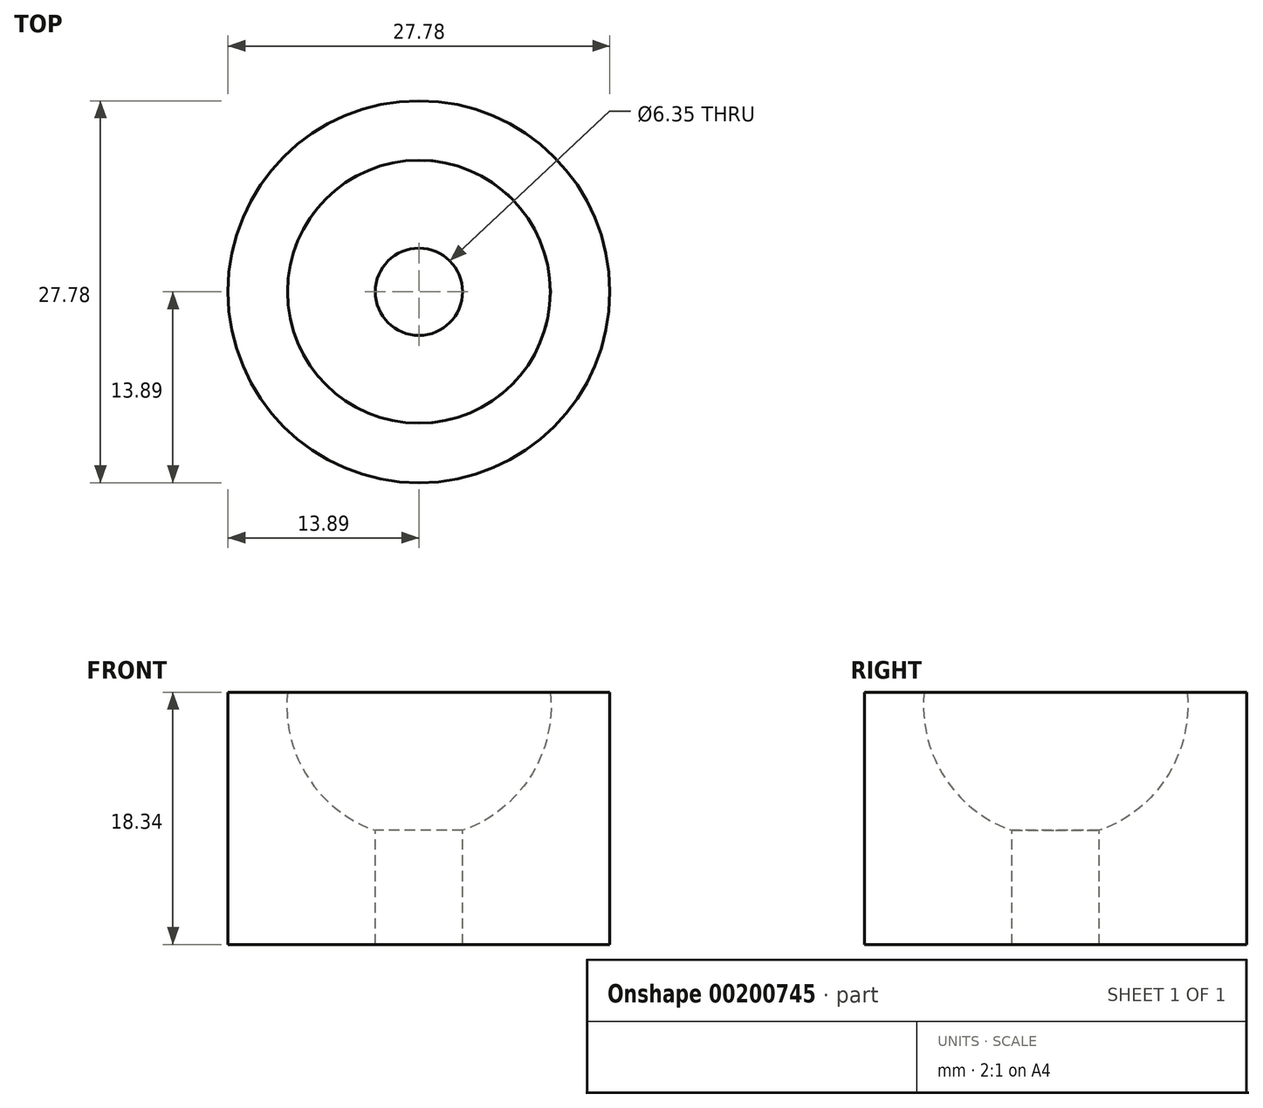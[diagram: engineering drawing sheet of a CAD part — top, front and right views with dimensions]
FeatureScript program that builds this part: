
annotation { "Feature Type Name" : "Feature", "Feature Type Description" : "" }
export const myFeature = defineFeature(function(context is Context, id is Id, definition is map)
    precondition{}
    {
        {
            var Q0;
            Q0=qCreatedBy(makeId("Front.planeOp"),FACE);
            var sketch = newSketch(context, id + "F0", { "sketchPlane" : qUnion([Q0])});
            skArc(sketch, "E0", {"start": v(-9.56, -0.66) * mm, "mid": v(-7.14, -8.08) * mm, "end": v(0, -11.25) * mm});
            skArc(sketch, "E1", {"start": v(0, -11.25) * mm, "mid": v(7.14, 4.8) * mm, "end": v(-9.56, -0.66) * mm, "construction": true});
            skLineSegment(sketch, "E2", {"start": v(-9.56, -0.66) * mm, "end": v(-13.9, -0.66) * mm});
            skLineSegment(sketch, "E3", {"start": v(-13.9, -0.66) * mm, "end": v(-13.9, -19) * mm});
            skLineSegment(sketch, "E4", {"start": v(-13.9, -19) * mm, "end": v(0, -19) * mm});
            skLineSegment(sketch, "E5", {"start": v(0, -11.25) * mm, "end": v(0, -19) * mm});
            skSolve(sketch);
        }
        {
            var Q0;
            Q0=makeQuery(id+"F0.imprint","IMPRINT",FACE,{"disambiguationData":[TD([[makeQuery(id+"F0.imprint","IMPRINT",EDGE,{"derivedFrom":sQuery(id+"F0.wireOp",EDGE,"E0")}),-1.0]])]});
            var Q1;
            Q1 = qSketchRegion(id + "F2", true);
            var Q2;
            Q2=sQuery(id+"F0.wireOp",EDGE,"E5");
            revolve(context, id + "F1", {"entities" : qUnion([Q0, Q1]), "axis" : qUnion([Q2]), "revolveType" : RevolveType.FULL});
        }
        {
            var Q0;
            Q0=qCreatedBy(makeId("Top.planeOp"),FACE);
            var sketch = newSketch(context, id + "F2", { "sketchPlane" : qUnion([Q0])});
            skPoint(sketch, "E6", {"position": v(0, 0) * mm});
            skSolve(sketch);
        }
        {
            var Q0;
            Q0=sQuery(id+"F2.wireOp",VERTEX,"E6");
            var Q1;
            Q1=makeQuery(id+"F1.opRevolve","SWEPT_BODY",BODY,{"disambiguationData":[OSD([sQuery(id+"F0.wireOp",EDGE,"E0"),sQuery(id+"F0.wireOp",EDGE,"E2"),sQuery(id+"F0.wireOp",EDGE,"E3"),sQuery(id+"F0.wireOp",EDGE,"E4"),sQuery(id+"F0.wireOp",EDGE,"E5")])]});
            hole(context, id + "F3", {"style" : HoleStyle.C_SINK, "endStyle" : HoleEndStyle.THROUGH, "holeDiameter" : 6.35 * mm, "cSinkDiameter" : 12.7 * mm, "cSinkAngle" : 90 * degree, "startFromSketch" : true, "locations" : qUnion([Q0]), "scope" : qUnion([Q1]), "isTappedThrough" : true});
        }
    });
